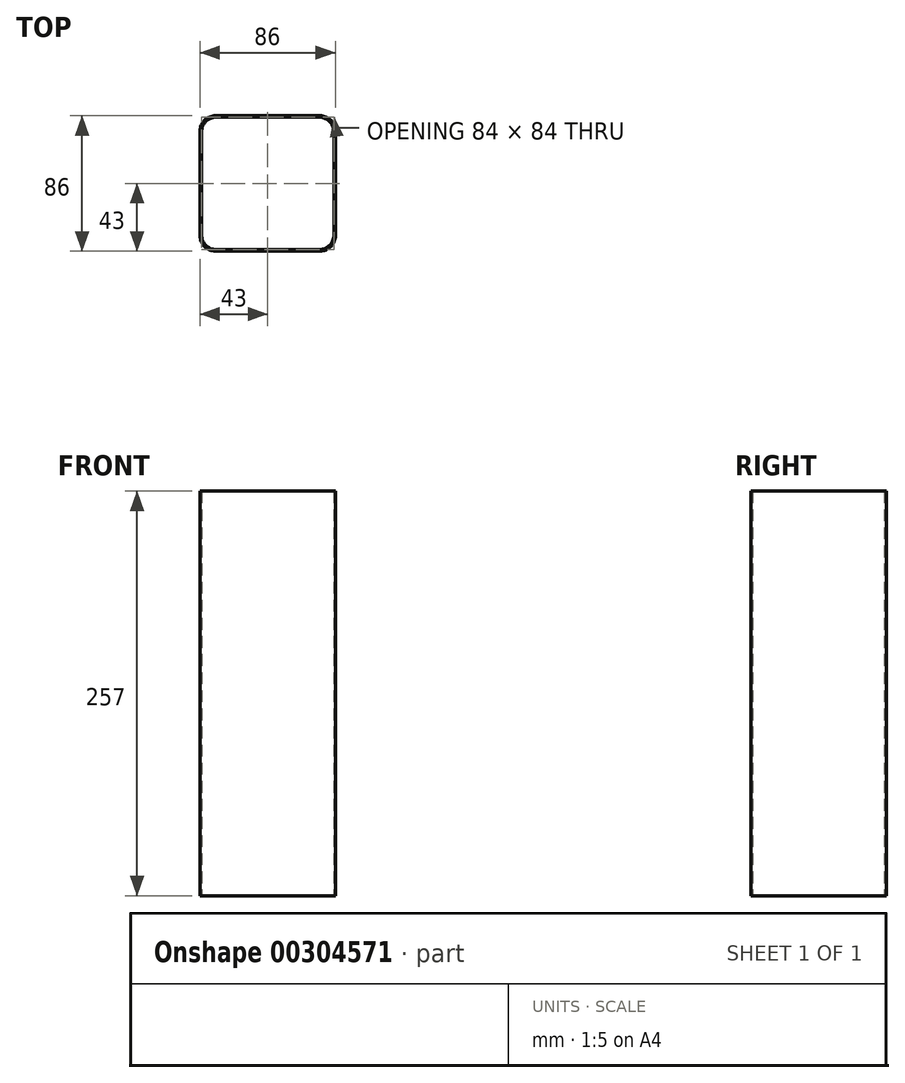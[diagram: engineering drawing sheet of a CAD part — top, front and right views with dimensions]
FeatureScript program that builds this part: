
annotation { "Feature Type Name" : "Feature", "Feature Type Description" : "" }
export const myFeature = defineFeature(function(context is Context, id is Id, definition is map)
    precondition{}
    {
        {
            var Q0;
            Q0=qCreatedBy(makeId("Top.planeOp"),FACE);
            var sketch = newSketch(context, id + "F0", { "sketchPlane" : qUnion([Q0])});
            skLineSegment(sketch, "E0.bottom", {"start": v(43, 43) * mm, "end": v(-43, 43) * mm});
            skLineSegment(sketch, "E0.top", {"start": v(43, -43) * mm, "end": v(-43, -43) * mm});
            skLineSegment(sketch, "E0.left", {"start": v(43, 43) * mm, "end": v(43, -43) * mm});
            skLineSegment(sketch, "E0.right", {"start": v(-43, 43) * mm, "end": v(-43, -43) * mm});
            skPoint(sketch, "E0.middle", {"position": v(0, 0) * mm});
            skSolve(sketch);
        }
        {
            var Q0;
            Q0=makeQuery(id+"F0.imprint","IMPRINT",FACE,{"disambiguationData":[TD([[makeQuery(id+"F0.imprint","IMPRINT",EDGE,{"derivedFrom":sQuery(id+"F0.wireOp",EDGE,"E0.bottom")}),1.0]])]});
            extrude(context, id + "F1", {"entities" : qUnion([Q0]), "depth" : 257 * mm});
        }
        {
            var Q0;
            Q0=makeQuery(id+"F1.opExtrude","SWEPT_EDGE",EDGE,{"disambiguationData":[OSD([sQuery(id+"F0.wireOp",EDGE,"E0.bottom"),sQuery(id+"F0.wireOp",EDGE,"E0.left")])]});
            var Q1;
            Q1=makeQuery(id+"F1.opExtrude","SWEPT_EDGE",EDGE,{"disambiguationData":[OSD([sQuery(id+"F0.wireOp",EDGE,"E0.top"),sQuery(id+"F0.wireOp",EDGE,"E0.right")])]});
            var Q2;
            Q2=makeQuery(id+"F1.opExtrude","SWEPT_EDGE",EDGE,{"disambiguationData":[OSD([sQuery(id+"F0.wireOp",EDGE,"E0.top"),sQuery(id+"F0.wireOp",EDGE,"E0.left")])]});
            var Q3;
            Q3=makeQuery(id+"F1.opExtrude","SWEPT_EDGE",EDGE,{"disambiguationData":[OSD([sQuery(id+"F0.wireOp",EDGE,"E0.bottom"),sQuery(id+"F0.wireOp",EDGE,"E0.right")])]});
            fillet(context, id + "F2", {"entities" : qUnion([Q0, Q1, Q2, Q3]), "radius" : 10 * mm, "tangentPropagation" : true, "allowEdgeOverflow" : false});
        }
        {
            var Q0;
            Q0=makeQuery(id+"F1.opExtrude","CAP_FACE",FACE,{"disambiguationData":[OSD([sQuery(id+"F0.wireOp",EDGE,"E0.bottom"),sQuery(id+"F0.wireOp",EDGE,"E0.top"),sQuery(id+"F0.wireOp",EDGE,"E0.left"),sQuery(id+"F0.wireOp",EDGE,"E0.right")])],"isStart":false});
            var Q1;
            Q1=makeQuery(id+"F1.opExtrude","CAP_FACE",FACE,{"disambiguationData":[OSD([sQuery(id+"F0.wireOp",EDGE,"E0.bottom"),sQuery(id+"F0.wireOp",EDGE,"E0.top"),sQuery(id+"F0.wireOp",EDGE,"E0.left"),sQuery(id+"F0.wireOp",EDGE,"E0.right")])],"isStart":true});
            shell(context, id + "F3", {"entities" : qUnion([Q0, Q1]), "thickness" : 1 * mm});
        }
    });
